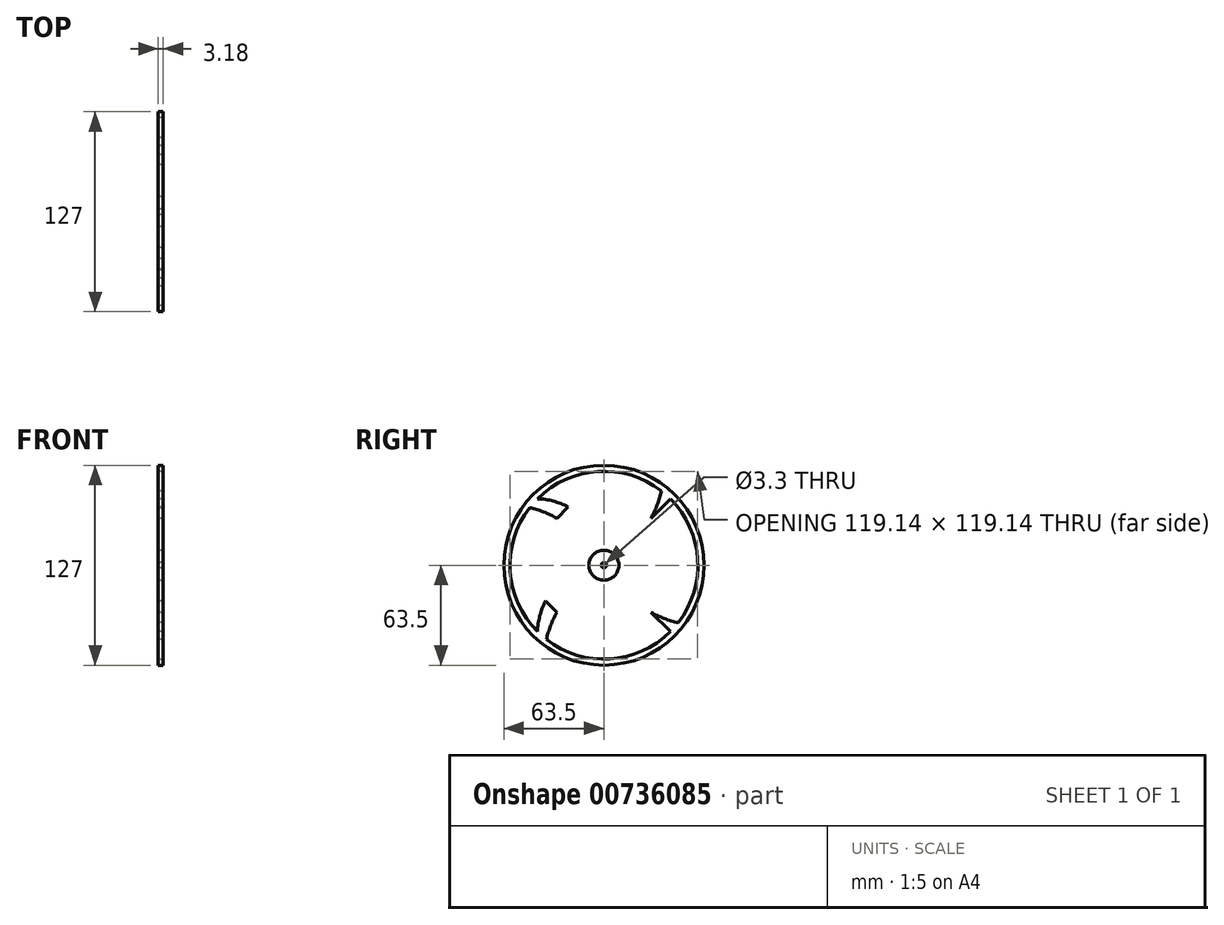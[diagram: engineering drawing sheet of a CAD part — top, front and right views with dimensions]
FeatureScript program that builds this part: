
annotation { "Feature Type Name" : "Feature", "Feature Type Description" : "" }
export const myFeature = defineFeature(function(context is Context, id is Id, definition is map)
    precondition{}
    {
        {
            var Q0;
            Q0=qCreatedBy(makeId("Right.planeOp"),FACE);
            var sketch = newSketch(context, id + "F0", { "sketchPlane" : qUnion([Q0])});
            skCircle(sketch, "E0", {"center": v(0, 0) * mm, "radius": 1.65 * mm});
            skCircle(sketch, "E1", {"center": v(0, 0) * mm, "radius": 63.5 * mm});
            skCircle(sketch, "E2", {"center": v(0, 0) * mm, "radius": 9.53 * mm});
            skLineSegment(sketch, "E3", {"start": v(1.65, 0) * mm, "end": v(9.53, 0) * mm});
            skLineSegment(sketch, "E4", {"start": v(9.53, 0) * mm, "end": v(0, 9.53) * mm});
            skLineSegment(sketch, "E5", {"start": v(0, 0) * mm, "end": v(6.74, 6.74) * mm});
            skLineSegment(sketch, "E6", {"start": v(0, 1.65) * mm, "end": v(0, 9.53) * mm});
            skLineSegment(sketch, "E7.MirrorCS", {"start": v(0, 0) * mm, "end": v(6.74, -6.74) * mm});
            skLineSegment(sketch, "E8.MirrorCS", {"start": v(0, -1.65) * mm, "end": v(0, -9.53) * mm});
            skLineSegment(sketch, "E9.MirrorCS", {"start": v(0, 0) * mm, "end": v(-6.74, -6.74) * mm});
            skLineSegment(sketch, "E10.MirrorCS", {"start": v(-1.65, 0) * mm, "end": v(-9.53, 0) * mm});
            skLineSegment(sketch, "E11.MirrorCS", {"start": v(0, 0) * mm, "end": v(-6.74, 6.74) * mm});
            skCircle(sketch, "E12", {"center": v(0, 0) * mm, "radius": 59.7 * mm});
            skLineSegment(sketch, "E13", {"start": v(0, 59.7) * mm, "end": v(-59.7, 0) * mm});
            skLineSegment(sketch, "E14", {"start": v(-59.7, 0) * mm, "end": v(0, -59.7) * mm});
            skLineSegment(sketch, "E15", {"start": v(0, -59.7) * mm, "end": v(59.7, 0) * mm});
            skLineSegment(sketch, "E16", {"start": v(59.69, 0) * mm, "end": v(0, 59.69) * mm});
            skLineSegment(sketch, "E17", {"start": v(29.84, 29.84) * mm, "end": v(37.03, 22.66) * mm});
            skLineSegment(sketch, "E18", {"start": v(29.84, 29.84) * mm, "end": v(42.2, 42.2) * mm});
            skLineSegment(sketch, "E19", {"start": v(42.2, 42.2) * mm, "end": v(36.49, 47.24) * mm});
            skLineSegment(sketch, "E20", {"start": v(29.85, -29.84) * mm, "end": v(22.66, -37.03) * mm});
            skLineSegment(sketch, "E21", {"start": v(29.85, -29.85) * mm, "end": v(42.2, -42.2) * mm});
            skLineSegment(sketch, "E22", {"start": v(42.2, -42.2) * mm, "end": v(47.24, -36.49) * mm});
            skLineSegment(sketch, "E23", {"start": v(-29.84, -29.84) * mm, "end": v(-42.2, -42.2) * mm});
            skLineSegment(sketch, "E24", {"start": v(-42.2, -42.2) * mm, "end": v(-36.49, -47.24) * mm});
            skLineSegment(sketch, "E25", {"start": v(-29.84, -29.85) * mm, "end": v(-37.03, -22.66) * mm});
            skLineSegment(sketch, "E26", {"start": v(-29.85, 29.85) * mm, "end": v(-42.2, 42.2) * mm});
            skLineSegment(sketch, "E27", {"start": v(-42.2, 42.2) * mm, "end": v(-47.24, 36.49) * mm});
            skLineSegment(sketch, "E28", {"start": v(-29.85, 29.84) * mm, "end": v(-22.66, 37.03) * mm});
            skArc(sketch, "E29", {"start": v(6.74, 6.74) * mm, "mid": v(25.93, 23.81) * mm, "end": v(36.49, 47.24) * mm});
            skArc(sketch, "E30", {"start": v(9.53, 0) * mm, "mid": v(32.66, 15.84) * mm, "end": v(42.2, 42.2) * mm});
            skArc(sketch, "E31", {"start": v(6.74, -6.74) * mm, "mid": v(23.81, -25.93) * mm, "end": v(47.24, -36.49) * mm});
            skArc(sketch, "E32", {"start": v(0, -9.53) * mm, "mid": v(15.84, -32.66) * mm, "end": v(42.2, -42.2) * mm});
            skArc(sketch, "E33", {"start": v(-6.74, -6.74) * mm, "mid": v(-25.93, -23.81) * mm, "end": v(-36.49, -47.24) * mm});
            skArc(sketch, "E34", {"start": v(-9.53, 0) * mm, "mid": v(-32.66, -15.84) * mm, "end": v(-42.2, -42.2) * mm});
            skArc(sketch, "E35", {"start": v(-6.74, 6.74) * mm, "mid": v(-23.81, 25.93) * mm, "end": v(-47.24, 36.49) * mm});
            skArc(sketch, "E36", {"start": v(0, 9.53) * mm, "mid": v(-15.84, 32.66) * mm, "end": v(-42.2, 42.2) * mm});
            skSolve(sketch);
        }
        {
            var Q0;
            {var subQ0=sQuery(id+"F0.wireOp",EDGE,"E3");Q0=makeQuery(id+"F0.imprint","IMPRINT",FACE,{"disambiguationData":[TD([[makeQuery(id+"F0.imprint","IMPRINT",EDGE,{"derivedFrom":subQ0}),-1.0]])]});}
            var Q1;
            {var subQ0=sQuery(id+"F0.wireOp",EDGE,"E3");Q1=makeQuery(id+"F0.imprint","IMPRINT",FACE,{"disambiguationData":[TD([[makeQuery(id+"F0.imprint","IMPRINT",EDGE,{"derivedFrom":subQ0}),1.0]])]});}
            var Q2;
            {var subQ0=sQuery(id+"F0.wireOp",EDGE,"E4");var subQ3=sQuery(id+"F0.wireOp",EDGE,"E5");var subQ5=makeQuery(id+"F0.imprint","INTERSECT",VERTEX,{"derivedFrom":[subQ0,subQ3]});Q2=makeQuery(id+"F0.imprint","IMPRINT",FACE,{"disambiguationData":[TD([[makeQuery(id+"F0.imprint","IMPRINT",EDGE,{"disambiguationData":[TD([[subQ5,-1.0]])],"derivedFrom":subQ3}),-1.0]])]});}
            var Q3;
            {var subQ0=sQuery(id+"F0.wireOp",EDGE,"E4");var subQ3=sQuery(id+"F0.wireOp",EDGE,"E5");var subQ5=makeQuery(id+"F0.imprint","INTERSECT",VERTEX,{"derivedFrom":[subQ0,subQ3]});Q3=makeQuery(id+"F0.imprint","IMPRINT",FACE,{"disambiguationData":[TD([[makeQuery(id+"F0.imprint","IMPRINT",EDGE,{"disambiguationData":[TD([[subQ5,-1.0]])],"derivedFrom":subQ3}),1.0]])]});}
            var Q4;
            {var subQ0=sQuery(id+"F0.wireOp",EDGE,"E6");Q4=makeQuery(id+"F0.imprint","IMPRINT",FACE,{"disambiguationData":[TD([[makeQuery(id+"F0.imprint","IMPRINT",EDGE,{"derivedFrom":subQ0}),-1.0]])]});}
            var Q5;
            {var subQ0=sQuery(id+"F0.wireOp",EDGE,"E6");Q5=makeQuery(id+"F0.imprint","IMPRINT",FACE,{"disambiguationData":[TD([[makeQuery(id+"F0.imprint","IMPRINT",EDGE,{"derivedFrom":subQ0}),1.0]])]});}
            var Q6;
            {var subQ0=sQuery(id+"F0.wireOp",EDGE,"E10.MirrorCS");Q6=makeQuery(id+"F0.imprint","IMPRINT",FACE,{"disambiguationData":[TD([[makeQuery(id+"F0.imprint","IMPRINT",EDGE,{"derivedFrom":subQ0}),-1.0]])]});}
            var Q7;
            {var subQ0=sQuery(id+"F0.wireOp",EDGE,"E10.MirrorCS");Q7=makeQuery(id+"F0.imprint","IMPRINT",FACE,{"disambiguationData":[TD([[makeQuery(id+"F0.imprint","IMPRINT",EDGE,{"derivedFrom":subQ0}),1.0]])]});}
            var Q8;
            {var subQ0=sQuery(id+"F0.wireOp",EDGE,"E8.MirrorCS");Q8=makeQuery(id+"F0.imprint","IMPRINT",FACE,{"disambiguationData":[TD([[makeQuery(id+"F0.imprint","IMPRINT",EDGE,{"derivedFrom":subQ0}),-1.0]])]});}
            var Q9;
            {var subQ5=sQuery(id+"F0.wireOp",EDGE,"E20");Q9=makeQuery(id+"F0.imprint","IMPRINT",FACE,{"disambiguationData":[TD([[makeQuery(id+"F0.imprint","IMPRINT",EDGE,{"derivedFrom":subQ5}),-1.0]])]});}
            var Q10;
            {var subQ5=sQuery(id+"F0.wireOp",EDGE,"E28");Q10=makeQuery(id+"F0.imprint","IMPRINT",FACE,{"disambiguationData":[TD([[makeQuery(id+"F0.imprint","IMPRINT",EDGE,{"derivedFrom":subQ5}),-1.0]])]});}
            var Q11;
            {var subQ5=sQuery(id+"F0.wireOp",EDGE,"E17");Q11=makeQuery(id+"F0.imprint","IMPRINT",FACE,{"disambiguationData":[TD([[makeQuery(id+"F0.imprint","IMPRINT",EDGE,{"derivedFrom":subQ5}),-1.0]])]});}
            var Q12;
            {var subQ5=sQuery(id+"F0.wireOp",EDGE,"E25");Q12=makeQuery(id+"F0.imprint","IMPRINT",FACE,{"disambiguationData":[TD([[makeQuery(id+"F0.imprint","IMPRINT",EDGE,{"derivedFrom":subQ5}),-1.0]])]});}
            var Q13;
            {var subQ0=sQuery(id+"F0.wireOp",EDGE,"E23");Q13=makeQuery(id+"F0.imprint","IMPRINT",FACE,{"disambiguationData":[TD([[makeQuery(id+"F0.imprint","IMPRINT",EDGE,{"derivedFrom":subQ0}),-1.0]])]});}
            var Q14;
            {var subQ0=sQuery(id+"F0.wireOp",EDGE,"E23");Q14=makeQuery(id+"F0.imprint","IMPRINT",FACE,{"disambiguationData":[TD([[makeQuery(id+"F0.imprint","IMPRINT",EDGE,{"derivedFrom":subQ0}),1.0]])]});}
            var Q15;
            Q15=makeQuery(id+"F0.imprint","IMPRINT",FACE,{"disambiguationData":[TD([[makeQuery(id+"F0.imprint","IMPRINT",EDGE,{"derivedFrom":sQuery(id+"F0.wireOp",EDGE,"E1")}),1.0]])]});
            var Q16;
            {var subQ0=sQuery(id+"F0.wireOp",EDGE,"E20");Q16=makeQuery(id+"F0.imprint","IMPRINT",FACE,{"disambiguationData":[TD([[makeQuery(id+"F0.imprint","IMPRINT",EDGE,{"derivedFrom":subQ0}),1.0]])]});}
            var Q17;
            {var subQ0=sQuery(id+"F0.wireOp",EDGE,"E21");Q17=makeQuery(id+"F0.imprint","IMPRINT",FACE,{"disambiguationData":[TD([[makeQuery(id+"F0.imprint","IMPRINT",EDGE,{"derivedFrom":subQ0}),1.0]])]});}
            var Q18;
            {var subQ0=sQuery(id+"F0.wireOp",EDGE,"E8.MirrorCS");Q18=makeQuery(id+"F0.imprint","IMPRINT",FACE,{"disambiguationData":[TD([[makeQuery(id+"F0.imprint","IMPRINT",EDGE,{"derivedFrom":subQ0}),1.0]])]});}
            var Q19;
            {var subQ0=sQuery(id+"F0.wireOp",EDGE,"E17");Q19=makeQuery(id+"F0.imprint","IMPRINT",FACE,{"disambiguationData":[TD([[makeQuery(id+"F0.imprint","IMPRINT",EDGE,{"derivedFrom":subQ0}),1.0]])]});}
            var Q20;
            {var subQ0=sQuery(id+"F0.wireOp",EDGE,"E18");Q20=makeQuery(id+"F0.imprint","IMPRINT",FACE,{"disambiguationData":[TD([[makeQuery(id+"F0.imprint","IMPRINT",EDGE,{"derivedFrom":subQ0}),1.0]])]});}
            var Q21;
            {var subQ0=sQuery(id+"F0.wireOp",EDGE,"E26");Q21=makeQuery(id+"F0.imprint","IMPRINT",FACE,{"disambiguationData":[TD([[makeQuery(id+"F0.imprint","IMPRINT",EDGE,{"derivedFrom":subQ0}),-1.0]])]});}
            var Q22;
            {var subQ0=sQuery(id+"F0.wireOp",EDGE,"E26");Q22=makeQuery(id+"F0.imprint","IMPRINT",FACE,{"disambiguationData":[TD([[makeQuery(id+"F0.imprint","IMPRINT",EDGE,{"derivedFrom":subQ0}),1.0]])]});}
            var Q23;
            {var subQ0=sQuery(id+"F0.wireOp",EDGE,"E27");Q23=makeQuery(id+"F0.imprint","IMPRINT",FACE,{"disambiguationData":[TD([[makeQuery(id+"F0.imprint","IMPRINT",EDGE,{"derivedFrom":subQ0}),-1.0]])]});}
            var Q24;
            {var subQ0=sQuery(id+"F0.wireOp",EDGE,"E24");Q24=makeQuery(id+"F0.imprint","IMPRINT",FACE,{"disambiguationData":[TD([[makeQuery(id+"F0.imprint","IMPRINT",EDGE,{"derivedFrom":subQ0}),-1.0]])]});}
            var Q25;
            {var subQ0=sQuery(id+"F0.wireOp",EDGE,"E22");Q25=makeQuery(id+"F0.imprint","IMPRINT",FACE,{"disambiguationData":[TD([[makeQuery(id+"F0.imprint","IMPRINT",EDGE,{"derivedFrom":subQ0}),-1.0]])]});}
            var Q26;
            {var subQ0=sQuery(id+"F0.wireOp",EDGE,"E19");Q26=makeQuery(id+"F0.imprint","IMPRINT",FACE,{"disambiguationData":[TD([[makeQuery(id+"F0.imprint","IMPRINT",EDGE,{"derivedFrom":subQ0}),-1.0]])]});}
            extrude(context, id + "F1", {"entities" : qUnion([Q0, Q1, Q2, Q3, Q4, Q5, Q6, Q7, Q8, Q9, Q10, Q11, Q12, Q13, Q14, Q15, Q16, Q17, Q18, Q19, Q20, Q21, Q22, Q23, Q24, Q25, Q26]), "depth" : 3.17 * mm, "offsetDistance" : 25.4 * mm});
        }
    });
